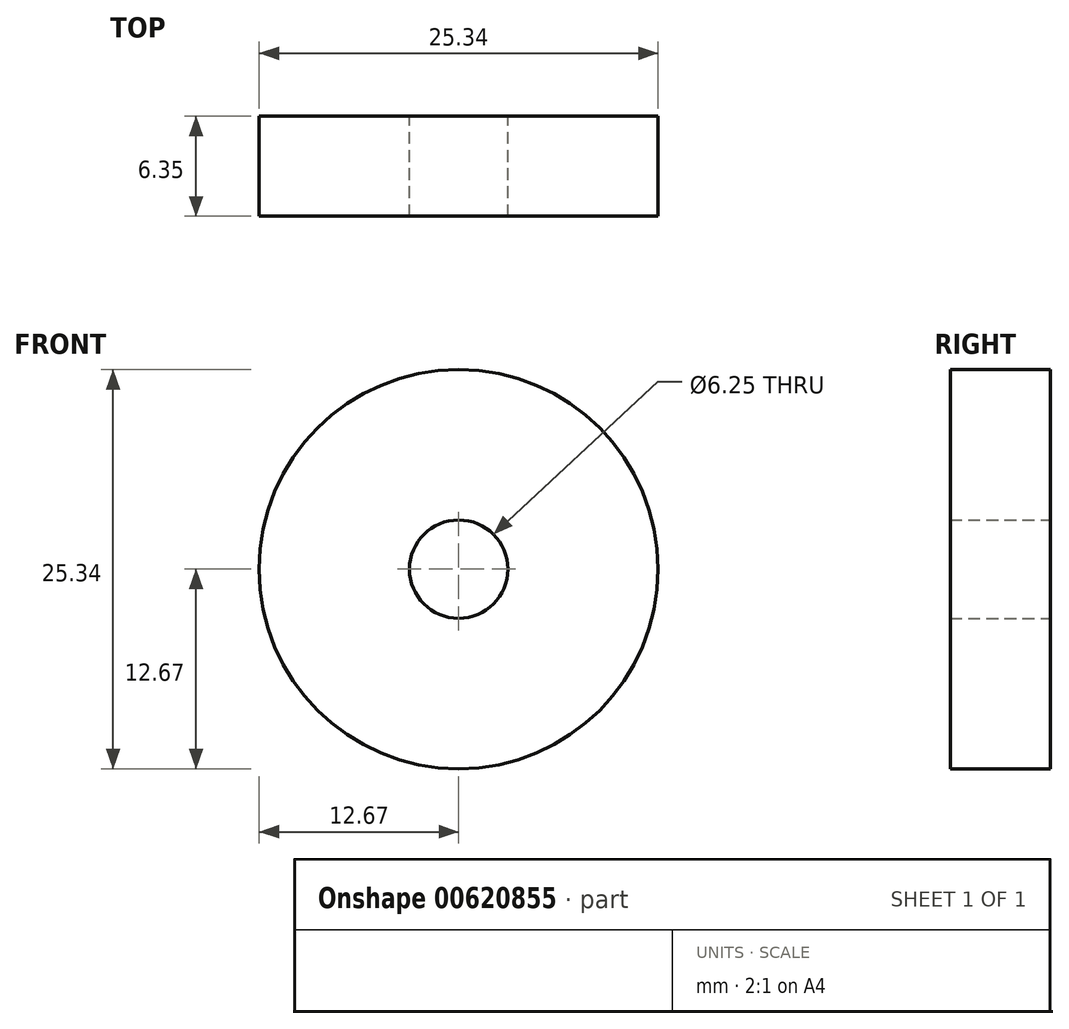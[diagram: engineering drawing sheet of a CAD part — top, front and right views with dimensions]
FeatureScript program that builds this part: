
annotation { "Feature Type Name" : "Feature", "Feature Type Description" : "" }
export const myFeature = defineFeature(function(context is Context, id is Id, definition is map)
    precondition{}
    {
        {
            var Q0;
            Q0=qCreatedBy(makeId("Front.planeOp"),FACE);
            var sketch = newSketch(context, id + "F0", { "sketchPlane" : qUnion([Q0])});
            skCircle(sketch, "E0", {"center": v(0, 0) * mm, "radius": 12.67 * mm});
            skCircle(sketch, "E1", {"center": v(0, 0) * mm, "radius": 3.12 * mm});
            skSolve(sketch);
        }
        {
            var Q0;
            Q0 = qSketchRegion(id + "F0", true);
            extrude(context, id + "F1", {"entities" : qUnion([Q0]), "depth" : 6.35 * mm, "offsetDistance" : 25.4 * mm});
        }
    });
